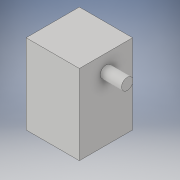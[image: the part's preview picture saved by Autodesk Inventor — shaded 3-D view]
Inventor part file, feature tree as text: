
AUTODESK INVENTOR PART (.ipt)
format: ipt  version: 2019 (Build 230136000, 136)  size: 100,352 bytes
history: native  units: mm
features: extrude x2, sketch x2, other x1
ambient origin geometry x8: Origin, YZ Plane, XZ Plane, XY Plane, X Axis, Y Axis, Z Axis, Center Point
bodies: Body1 (feature_tree)
feature tree (5):
  other  "Твердое тело1"
  extrude  "Выдавливание1"  Depth=15.0mm
  extrude  "Выдавливание2"  Depth=10.0mm
  sketch  "Эскиз1"
  sketch  "Эскиз2"
